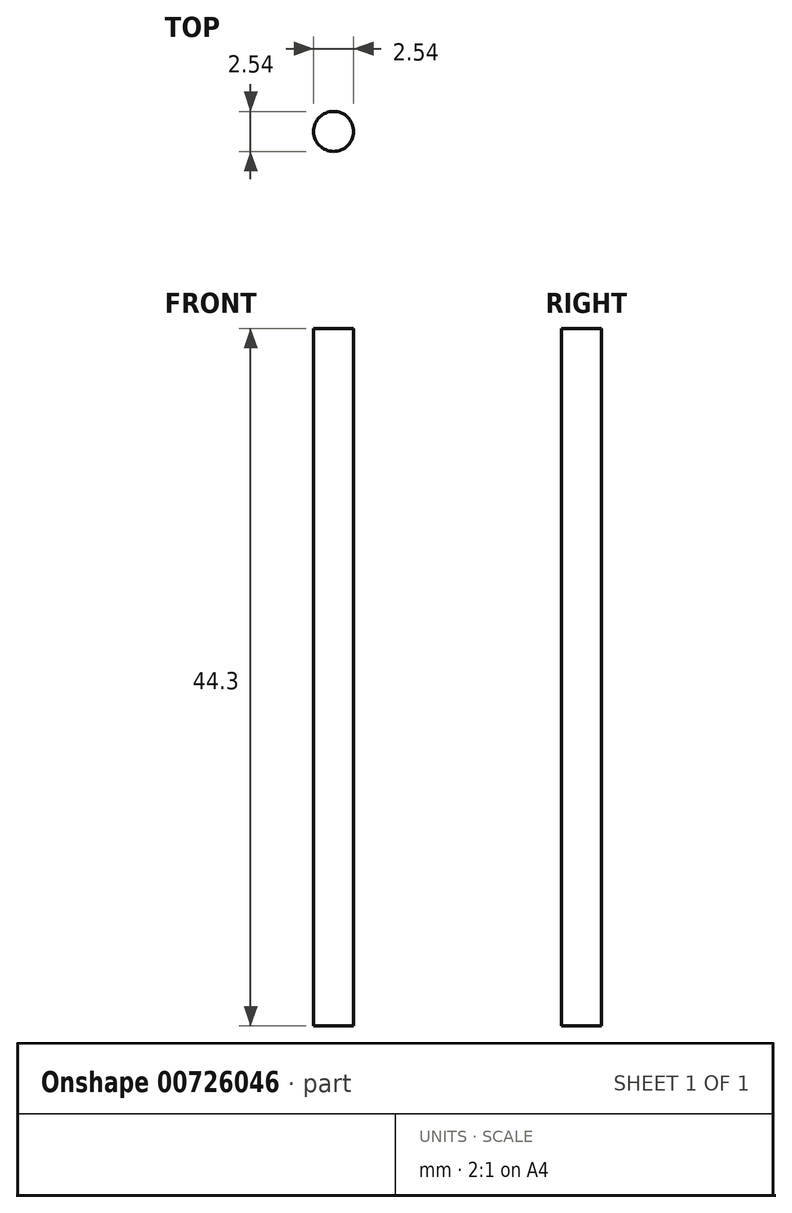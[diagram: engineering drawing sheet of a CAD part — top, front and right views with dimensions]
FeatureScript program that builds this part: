
annotation { "Feature Type Name" : "Feature", "Feature Type Description" : "" }
export const myFeature = defineFeature(function(context is Context, id is Id, definition is map)
    precondition{}
    {
        {
            var Q0;
            Q0=qCreatedBy(makeId("Top.planeOp"),FACE);
            var sketch = newSketch(context, id + "F0", { "sketchPlane" : qUnion([Q0])});
            skCircle(sketch, "E0", {"center": v(-28.55, 24.85) * mm, "radius": 1.27 * mm});
            skSolve(sketch);
        }
        {
            var Q0;
            Q0=makeQuery(id+"F0.imprint","IMPRINT",FACE,{"disambiguationData":[TD([[makeQuery(id+"F0.imprint","IMPRINT",EDGE,{"derivedFrom":sQuery(id+"F0.wireOp",EDGE,"E0")}),1.0]])]});
            extrude(context, id + "F1", {"entities" : qUnion([Q0]), "depth" : 44.3 * mm, "offsetDistance" : 25.4 * mm});
        }
    });
